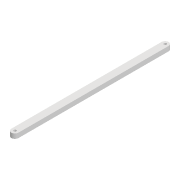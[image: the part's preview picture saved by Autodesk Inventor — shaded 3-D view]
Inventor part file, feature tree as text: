
AUTODESK INVENTOR PART (.ipt)
format: ipt  version: 2022 (Build 260153000, 153)  size: 89,600 bytes
history: native  units: mm
features: extrude x1, sketch x1
ambient origin geometry x8: Origin, YZ Plane, XZ Plane, XY Plane, X Axis, Y Axis, Z Axis, Center Point
bodies: Solid1 (feature_tree)
feature tree (2):
  extrude  "Extrusion1"  Depth=4.0mm
  sketch  "Sketch1"  dims[d0=2.2mm d1=2.2mm d2=6.0mm d3=128.523mm d6=4.0mm d7=0.0mm]
